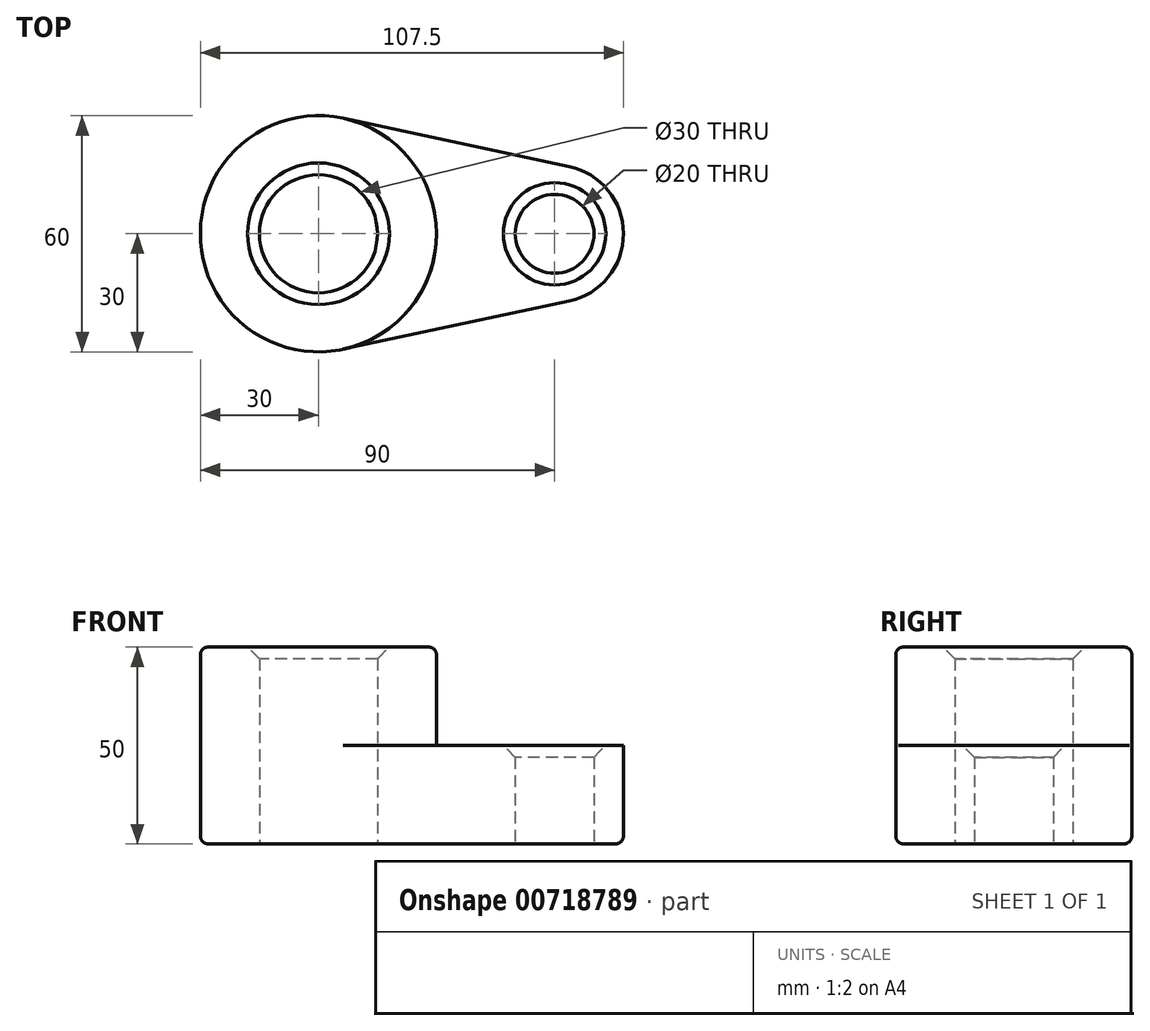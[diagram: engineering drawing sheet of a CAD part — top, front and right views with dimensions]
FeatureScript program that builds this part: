
annotation { "Feature Type Name" : "Feature", "Feature Type Description" : "" }
export const myFeature = defineFeature(function(context is Context, id is Id, definition is map)
    precondition{}
    {
        {
            var Q0;
            Q0=qCreatedBy(makeId("Top.planeOp"),FACE);
            var sketch = newSketch(context, id + "F0", { "sketchPlane" : qUnion([Q0])});
            skCircle(sketch, "E0", {"center": v(0, 0) * mm, "radius": 30 * mm});
            skCircle(sketch, "E1", {"center": v(60, 0) * mm, "radius": 17.5 * mm});
            skLineSegment(sketch, "E2", {"start": v(6.25, 29.34) * mm, "end": v(63.65, 17.12) * mm});
            skLineSegment(sketch, "E3", {"start": v(6.25, -29.34) * mm, "end": v(63.65, -17.12) * mm});
            skCircle(sketch, "E4", {"center": v(0, 0) * mm, "radius": 15 * mm});
            skCircle(sketch, "E5", {"center": v(60, 0) * mm, "radius": 10 * mm});
            skSolve(sketch);
        }
        {
            var Q0;
            Q0 = qSketchRegion(id + "F0", true);
            extrude(context, id + "F1", {"entities" : qUnion([Q0]), "depth" : 25 * mm, "offsetDistance" : 25 * mm});
        }
        {
            var Q0;
            Q0=makeQuery(id+"F0.imprint","IMPRINT",FACE,{"disambiguationData":[TD([[makeQuery(id+"F0.imprint","IMPRINT",EDGE,{"derivedFrom":sQuery(id+"F0.wireOp",EDGE,"E4")}),-1.0]])]});
            extrude(context, id + "F2", {"entities" : qUnion([Q0]), "operationType" : NewBodyOperationType.ADD, "depth" : 50 * mm, "offsetDistance" : 25 * mm});
        }
        {
            var Q0;
            Q0=makeQuery(id+"F2.opExtrude","CAP_EDGE",EDGE,{"disambiguationData":[OSD([sQuery(id+"F0.wireOp",EDGE,"E0")])],"isStart":false});
            var Q1;
            Q1=makeQuery(id+"F1.opExtrude","CAP_EDGE",EDGE,{"disambiguationData":[OSD([sQuery(id+"F0.wireOp",EDGE,"E3")])],"isStart":true});
            fillet(context, id + "F3", {"entities" : qUnion([Q0, Q1]), "radius" : 2 * mm, "tangentPropagation" : true, "allowEdgeOverflow" : false});
        }
        {
            var Q0;
            Q0=makeQuery(id+"F1.opExtrude","CAP_EDGE",EDGE,{"disambiguationData":[OSD([sQuery(id+"F0.wireOp",EDGE,"E5")])],"isStart":false});
            var Q1;
            Q1=makeQuery(id+"F2.opExtrude","CAP_EDGE",EDGE,{"disambiguationData":[OSD([sQuery(id+"F0.wireOp",EDGE,"E4")])],"isStart":false});
            chamfer(context, id + "F4", {"entities" : qUnion([Q0, Q1]), "width" : 3 * mm, "tangentPropagation" : true});
        }
    });
